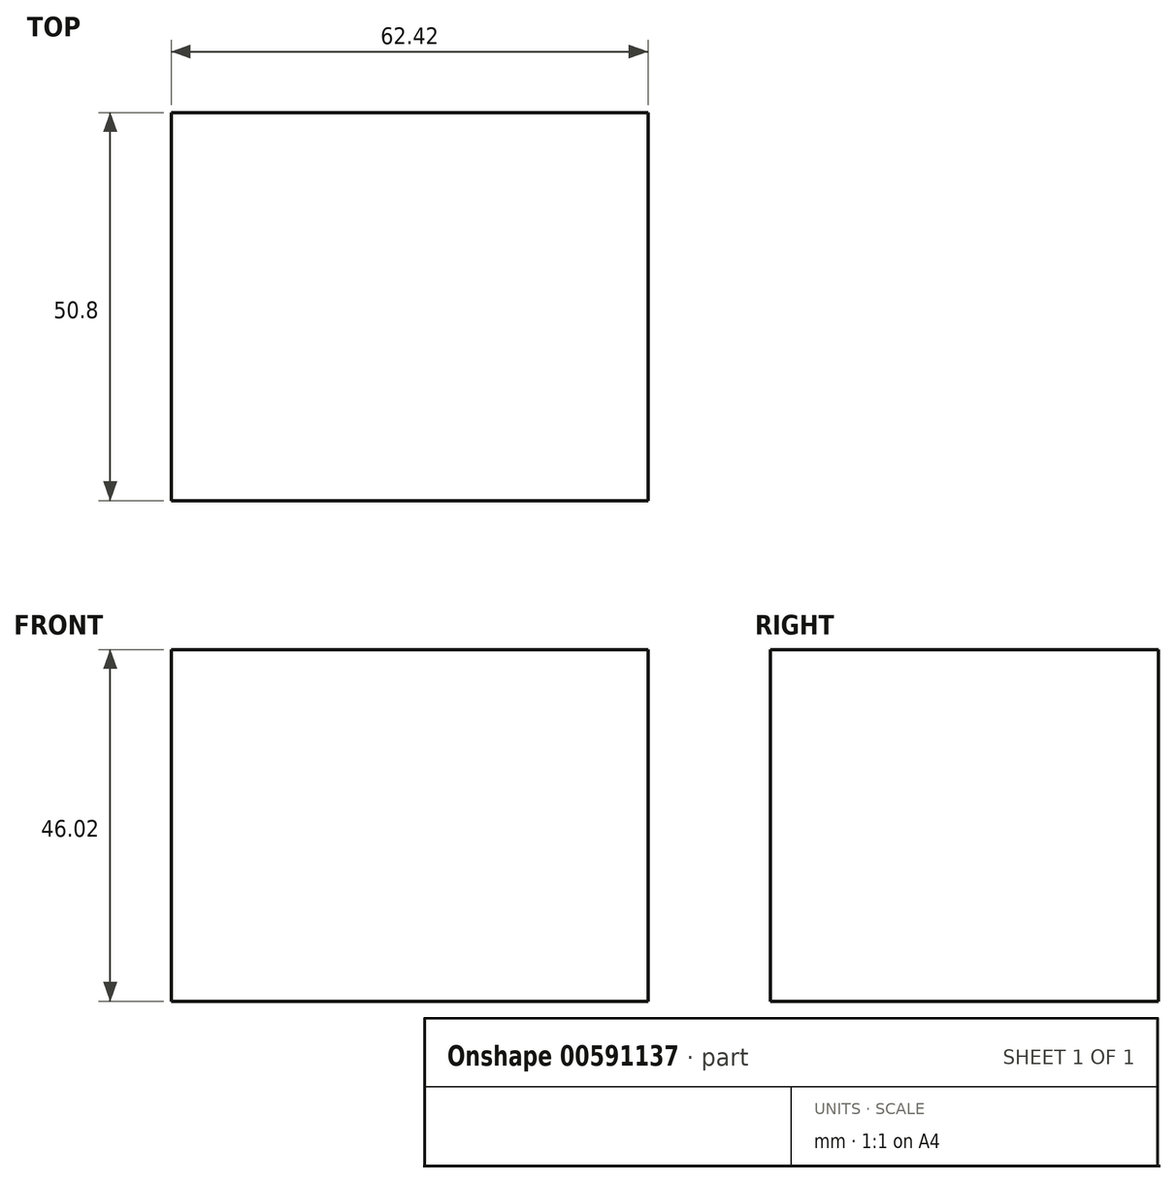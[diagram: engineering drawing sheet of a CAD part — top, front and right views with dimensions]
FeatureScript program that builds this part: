
annotation { "Feature Type Name" : "Feature", "Feature Type Description" : "" }
export const myFeature = defineFeature(function(context is Context, id is Id, definition is map)
    precondition{}
    {
        {
            var Q0;
            Q0=qCreatedBy(makeId("Front.planeOp"),FACE);
            var sketch = newSketch(context, id + "F0", { "sketchPlane" : qUnion([Q0])});
            skLineSegment(sketch, "E0.bottom", {"start": v(31.2, 23.01) * mm, "end": v(-31.2, 23.01) * mm});
            skLineSegment(sketch, "E0.top", {"start": v(31.2, -23.01) * mm, "end": v(-31.2, -23.01) * mm});
            skLineSegment(sketch, "E0.left", {"start": v(31.2, 23.01) * mm, "end": v(31.2, -23.01) * mm});
            skLineSegment(sketch, "E0.right", {"start": v(-31.2, 23.01) * mm, "end": v(-31.2, -23.01) * mm});
            skPoint(sketch, "E0.middle", {"position": v(0, 0) * mm});
            skSolve(sketch);
        }
        {
            var Q0;
            Q0 = qSketchRegion(id + "F0", true);
            extrude(context, id + "F1", {"entities" : qUnion([Q0]), "depth" : 50.8 * mm, "offsetDistance" : 25.4 * mm});
        }
    });
